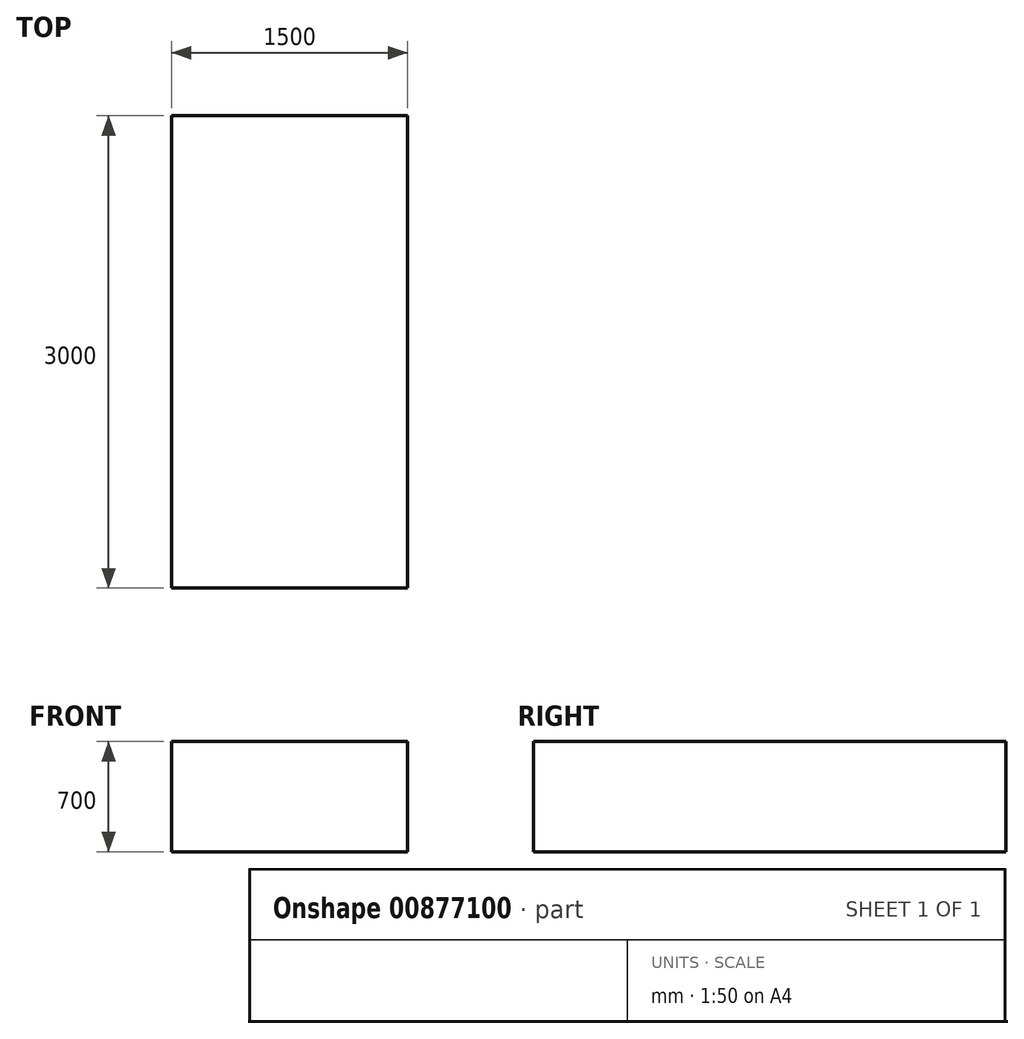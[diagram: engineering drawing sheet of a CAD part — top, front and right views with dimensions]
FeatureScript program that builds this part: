
annotation { "Feature Type Name" : "Feature", "Feature Type Description" : "" }
export const myFeature = defineFeature(function(context is Context, id is Id, definition is map)
    precondition{}
    {
        {
            var Q0;
            Q0=qCreatedBy(makeId("Top.planeOp"),FACE);
            var sketch = newSketch(context, id + "F0", { "sketchPlane" : qUnion([Q0])});
            skLineSegment(sketch, "E0.bottom", {"start": v(750, 1500) * mm, "end": v(-750, 1500) * mm});
            skLineSegment(sketch, "E0.top", {"start": v(750, -1500) * mm, "end": v(-750, -1500) * mm});
            skLineSegment(sketch, "E0.left", {"start": v(750, 1500) * mm, "end": v(750, -1500) * mm});
            skLineSegment(sketch, "E0.right", {"start": v(-750, 1500) * mm, "end": v(-750, -1500) * mm});
            skPoint(sketch, "E0.middle", {"position": v(0, 0) * mm});
            skSolve(sketch);
        }
        {
            var Q0;
            Q0=makeQuery(id+"F0.imprint","IMPRINT",FACE,{"disambiguationData":[TD([[makeQuery(id+"F0.imprint","IMPRINT",EDGE,{"derivedFrom":sQuery(id+"F0.wireOp",EDGE,"E0.bottom")}),1.0]])]});
            extrude(context, id + "F1", {"entities" : qUnion([Q0]), "depth" : 700 * mm, "offsetDistance" : 25 * mm});
        }
    });
